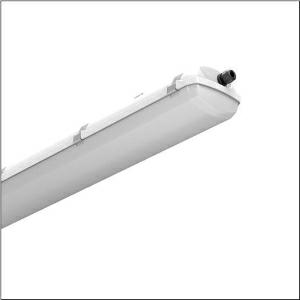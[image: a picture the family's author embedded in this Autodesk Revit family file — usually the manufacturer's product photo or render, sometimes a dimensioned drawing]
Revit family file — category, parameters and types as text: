
# Revit family: monsun_ex_51fxb17p6c0a
name_source: partatom
category: Lighting Fixtures
units: mm (PartAtom-declared; Revit-internal decimal feet)

## family parameters
Cut with Voids When Loaded = No
Host = Face
Light Source = No
Part Type = Normal
Room Calculation Point = No
Round Connector Dimension = Use Diameter
Shared = No

## types (1)
- Monsun Ex (1 x LED, 14960 lm, 94.7 W, 6500K)
    Apparent Load = 95 VA
    CIE Flux Codes = 61 86 97 98 100
    Color Rendering = 80
    Color Temperature = 6500K
    Default Elevation = 1800 mm
    Description = Monsun Ex, damp-proof luminaire, primary optical cover: cover, of PC, UV-stabilised, opal, light emission: direct distribution, primary light characteristic: symmetric, installation type: surface-mounted, LED, rated luminous flux: 14.960lm, luminous efficacy: 158lm/W, light colour: 865, colour temperature: 6500K, control gear: ON/OFF, with terminal, 3-pole, max. 2.5mm², through-wiring: 5x 2.5mm², mains connection: 220..240V, AC, 50/60Hz, rated input power: 95W, housing, of PC, light grey (RAL 7035), incl. blanking plug, incl. 2x Ex cable gland M20 for cable diameter 7..12mm with sealing, length: 1.580mm, width: 155mm, height: 105mm, clip for enclosure, of stainless steel, protection rating (complete): IP66, insulation class (complete): insulation class I (protective earthing), certification: CE, explosion class: zone2,22 II 3G Ex nR IIC T6 GC, II 3D Ex tc IIIC T80°C Dc, impact resistance: IK10, permissible operating ambient temperature: -20..+40°C, LABS conformity tested according to VDMA 24364:2018-05, contact your sales advisor before using the luminaires in applications with unclear chemical exposure, large temperature fluctuations or condensation-forming humidity, packaging unit: 1 piece
    Height = 105 mm
    Lamp = 1 x LED
    Lamp Light Flux = 14960 lm
    Lamp Power = 94.7 W
    Lamp count = 1
    Length = 1580 mm
    Luminous efficacy = 158 lm/W
    Manufacturer = Siteco
    ModVariant = No
    Model = 51FXB17P6C0A
    Mounting Place = Ceiling
    Mounting Type = Surface mounted
    Number of Poles = 1
    OnlyDefault = Yes
    Power Factor = 1
    Product Name = Monsun Ex
    Product group = damp-proof luminaire
    ProductGroupID = 300
    Protection Class = Protection class I
    Protection Degree = IP 66
    RLX_Detail_Level = 1
    RLX_Emergency_Light_Flux = 0 lm
    RLX_Emergency_Type = 0
    RLX_Emergency_Type_DB = No
    RlxData = <blob elided: 41785 chars, md5=08eb554a>
    Socket = socket
    Standby Power = 0 W
    System Light Flux = 14960 lm
    System Power = 95 W
    Type Comments = Product without accessories
    Type Image = l_1258882.jpg
    URL = http://relux.com
    VarID = ---
    Voltage = 0 V
    Weight = 0.00 kg
    Width = 155 mm

## geometry (parser evidence)
native form markers: Blend x4, Sweep x10
no freeform markers — native parametric forms only
